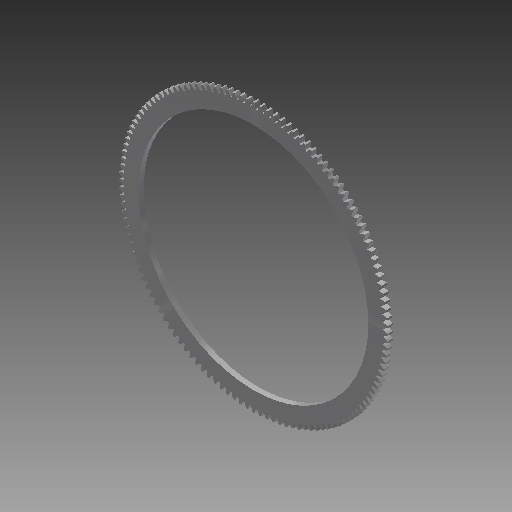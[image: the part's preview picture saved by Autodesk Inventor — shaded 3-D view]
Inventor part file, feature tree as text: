
AUTODESK INVENTOR PART (.ipt)
format: ipt  version: 2017 (Build 210142000, 142)  size: 644,096 bytes
history: native  units: mm (DEFAULTED — no unit token found)
features: plane x3, other x3, sketch x3, extrude x2
ambient origin geometry x8: Origin, YZ Plane, XZ Plane, XY Plane, X Axis, Y Axis, Z Axis, Center Point
bodies: Solid1 (feature_tree)
feature tree (11):
  extrude  "Extrusion1"  Depth=6.35mm TaperAngle=0.0deg
  plane  "Work Plane1"
  plane  "Work Plane2"
  plane  "Work Plane3"
  other  "Spur Gear"
  extrude  "Extrusion2"  Depth=76.2mm TaperAngle=0.0deg
  sketch  "Sketch1"  dims[d0=330.2mm d1=6.35mm d2=0.0mm]
  sketch  "Sketch2"  dims[d3=325.12mm d4=76.2mm d5=0.0mm]
  other  "Srf1"
  sketch  "Sketch3"  dims[d6=0.0mm d7=0.245437mm d9=0.0mm d14=0.0mm d15=181.61mm d16=0.0mm d17=0.0mm d18=0.0mm d19=181.61mm d20=282.575mm d21=25.4mm d22=0.0mm]
  other  "Pitch Diameter"
